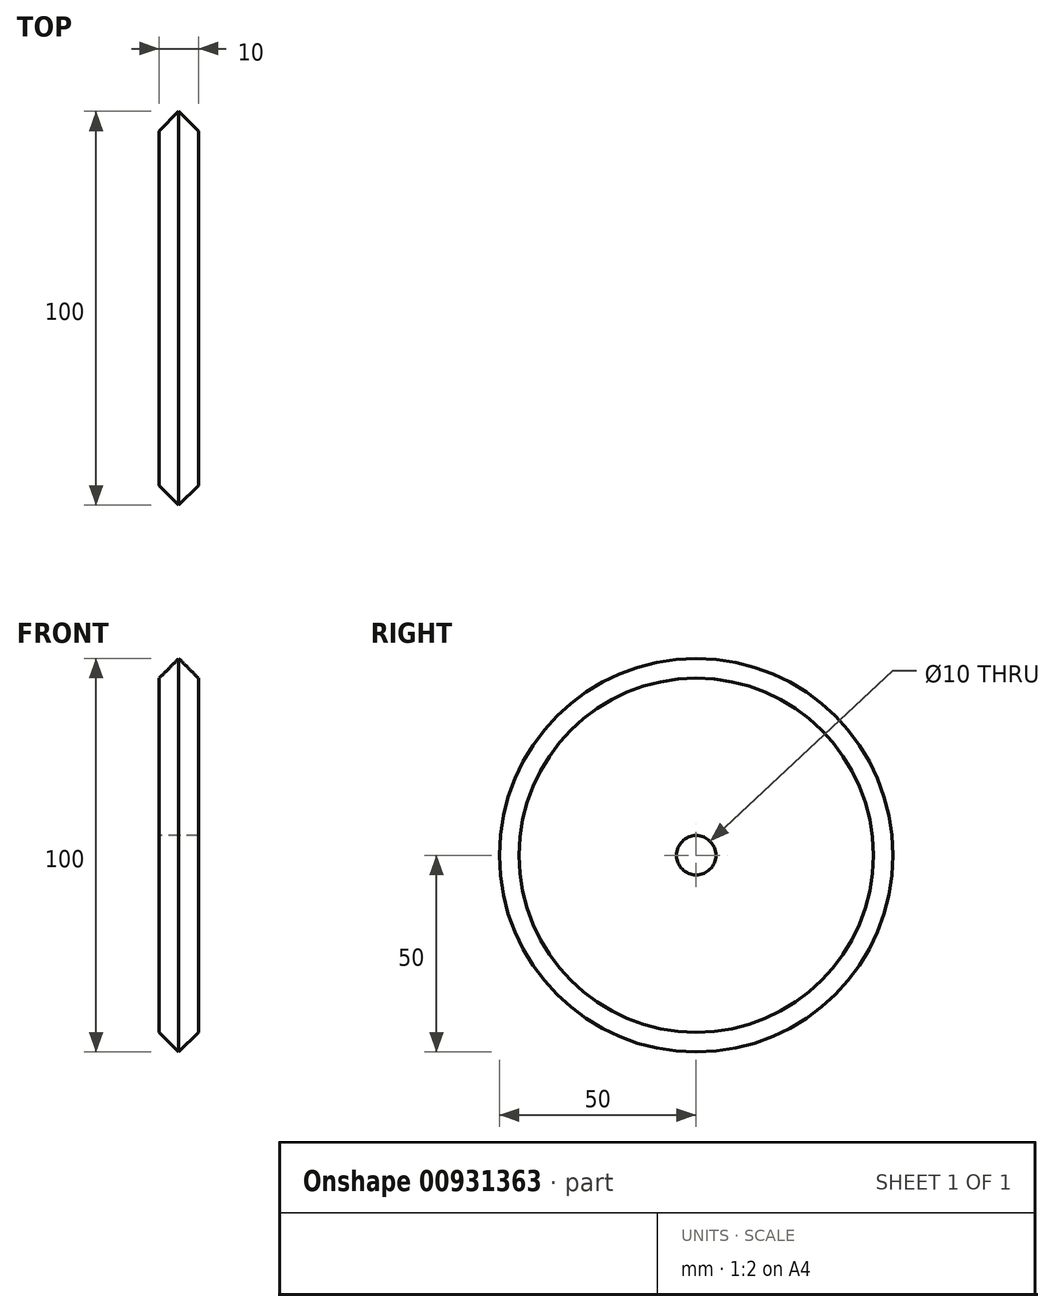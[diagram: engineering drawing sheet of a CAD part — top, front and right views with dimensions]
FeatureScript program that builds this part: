
annotation { "Feature Type Name" : "Feature", "Feature Type Description" : "" }
export const myFeature = defineFeature(function(context is Context, id is Id, definition is map)
    precondition{}
    {
        {
            var Q0;
            Q0=qCreatedBy(makeId("Front.planeOp"),FACE);
            var sketch = newSketch(context, id + "F0", { "sketchPlane" : qUnion([Q0])});
            skLineSegment(sketch, "E0", {"start": v(-93.45, 0) * mm, "end": v(93.45, 0) * mm, "construction": true});
            skLineSegment(sketch, "E1", {"start": v(0, 0) * mm, "end": v(0, 105.7) * mm, "construction": true});
            skLineSegment(sketch, "E2", {"start": v(-5, 5) * mm, "end": v(-5, 45) * mm});
            skLineSegment(sketch, "E3", {"start": v(-5, 45) * mm, "end": v(0, 50) * mm});
            skLineSegment(sketch, "E4", {"start": v(0, 50) * mm, "end": v(5, 45) * mm});
            skLineSegment(sketch, "E5", {"start": v(5, 45) * mm, "end": v(5, 5) * mm});
            skLineSegment(sketch, "E6", {"start": v(5, 5) * mm, "end": v(-5, 5) * mm});
            skSolve(sketch);
        }
        {
            var Q0;
            Q0 = qSketchRegion(id + "F0", true);
            var Q1;
            Q1=sQuery(id+"F0.wireOp",EDGE,"E0");
            revolve(context, id + "F1", {"surfaceOperationType" : NewSurfaceOperationType.NEW, "entities" : qUnion([Q0]), "axis" : qUnion([Q1]), "revolveType" : RevolveType.FULL});
        }
    });
